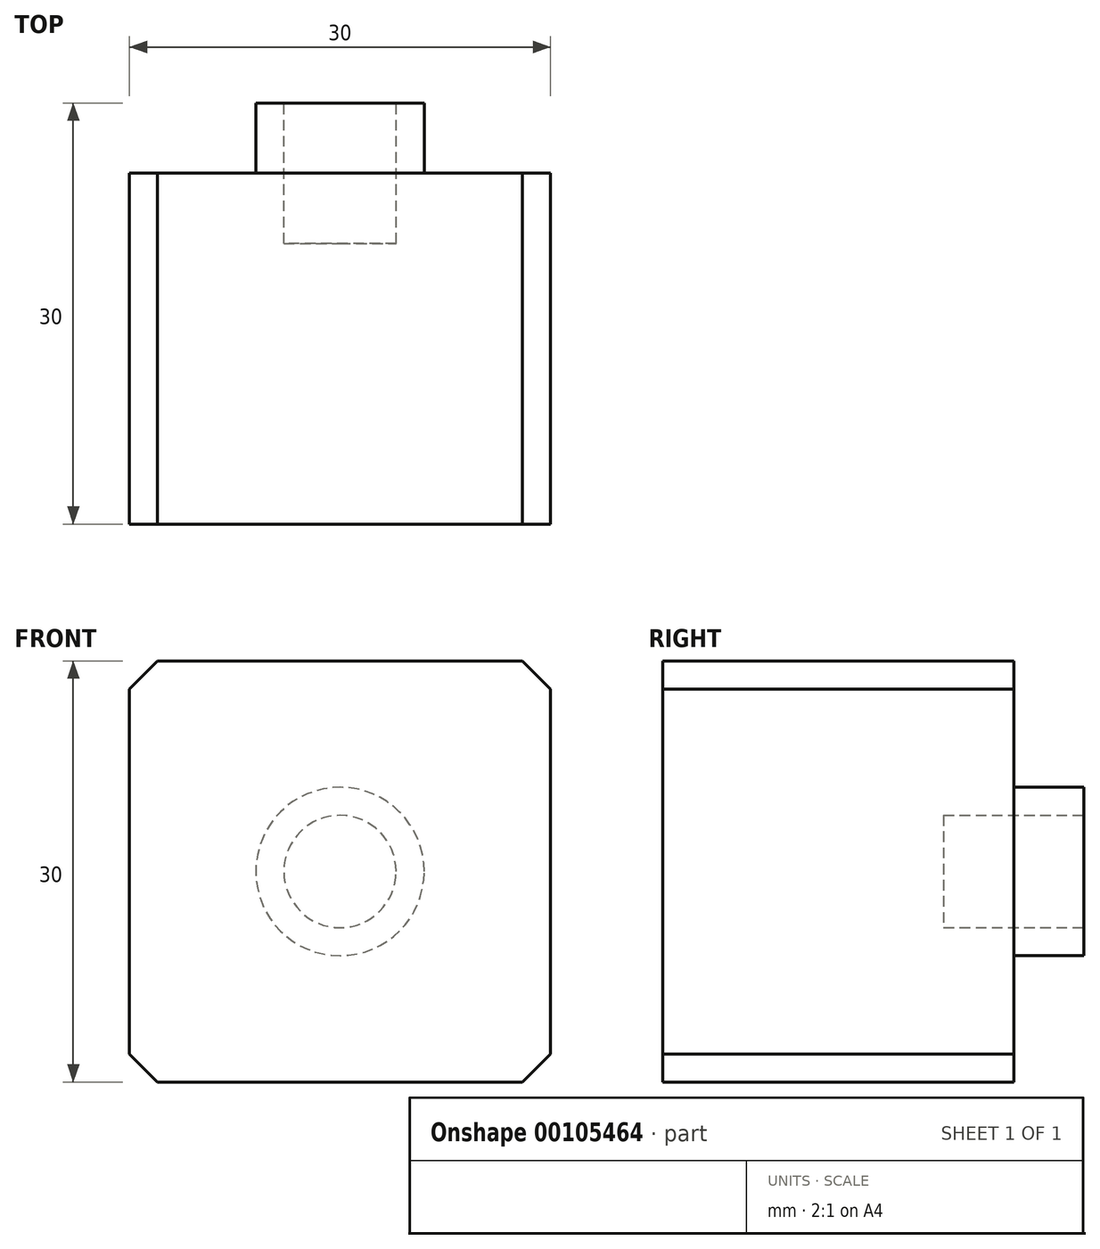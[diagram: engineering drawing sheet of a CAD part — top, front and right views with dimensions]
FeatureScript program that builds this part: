
annotation { "Feature Type Name" : "Feature", "Feature Type Description" : "" }
export const myFeature = defineFeature(function(context is Context, id is Id, definition is map)
    precondition{}
    {
        {
            var Q0;
            Q0=qCreatedBy(makeId("Front.planeOp"),FACE);
            var sketch = newSketch(context, id + "F0", { "sketchPlane" : qUnion([Q0])});
            skLineSegment(sketch, "E0.bottom", {"start": v(-12.17, 11.48) * mm, "end": v(17.83, 11.48) * mm});
            skLineSegment(sketch, "E0.top", {"start": v(-12.17, -18.52) * mm, "end": v(17.83, -18.52) * mm});
            skLineSegment(sketch, "E0.left", {"start": v(-12.17, 11.48) * mm, "end": v(-12.17, -18.52) * mm});
            skLineSegment(sketch, "E0.right", {"start": v(17.83, 11.48) * mm, "end": v(17.83, -18.52) * mm});
            skSolve(sketch);
        }
        {
            var Q0;
            Q0=makeQuery(id+"F0.imprint","IMPRINT",FACE,{"disambiguationData":[TD([[makeQuery(id+"F0.imprint","IMPRINT",EDGE,{"derivedFrom":sQuery(id+"F0.wireOp",EDGE,"E0.bottom")}),-1.0]])]});
            extrude(context, id + "F1", {"entities" : qUnion([Q0]), "depth" : 25 * mm});
        }
        {
            var Q0;
            Q0=makeQuery(id+"F1.opExtrude","CAP_FACE",FACE,{"disambiguationData":[OSD([sQuery(id+"F0.wireOp",EDGE,"E0.bottom"),sQuery(id+"F0.wireOp",EDGE,"E0.top"),sQuery(id+"F0.wireOp",EDGE,"E0.left"),sQuery(id+"F0.wireOp",EDGE,"E0.right")])],"isStart":true});
            var sketch = newSketch(context, id + "F2", { "sketchPlane" : qUnion([Q0])});
            skCircle(sketch, "E1", {"center": v(-2.83, -3.52) * mm, "radius": 4 * mm});
            skPoint(sketch, "E1.centerSnap0", {"position": v(12.17, -3.52) * mm});
            skPoint(sketch, "E1.centerSnap1", {"position": v(-2.83, 11.48) * mm});
            skSolve(sketch);
        }
        {
            var Q0;
            Q0=makeQuery(id+"F1.opExtrude","CAP_FACE",FACE,{"disambiguationData":[OSD([sQuery(id+"F0.wireOp",EDGE,"E0.bottom"),sQuery(id+"F0.wireOp",EDGE,"E0.top"),sQuery(id+"F0.wireOp",EDGE,"E0.left"),sQuery(id+"F0.wireOp",EDGE,"E0.right")])],"isStart":true});
            var sketch = newSketch(context, id + "F3", { "sketchPlane" : qUnion([Q0])});
            skCircle(sketch, "E2", {"center": v(-2.83, -3.52) * mm, "radius": 6 * mm});
            skPoint(sketch, "E2.centerSnap0", {"position": v(-2.83, 11.48) * mm});
            skPoint(sketch, "E2.centerSnap1", {"position": v(12.17, -3.52) * mm});
            skSolve(sketch);
        }
        {
            var Q0;
            Q0=makeQuery(id+"F3.imprint","IMPRINT",FACE,{"disambiguationData":[TD([[makeQuery(id+"F3.imprint","IMPRINT",EDGE,{"derivedFrom":sQuery(id+"F3.wireOp",EDGE,"E2")}),1.0]])]});
            var Q1;
            Q1=sQuery(id+"F3.wireOp",EDGE,"E2");
            extrude(context, id + "F4", {"entities" : qUnion([Q0]), "operationType" : NewBodyOperationType.ADD, "surfaceEntities" : qUnion([Q1]), "depth" : 5 * mm});
        }
        {
            var Q0;
            Q0=makeQuery(id+"F1.opExtrude","SWEPT_EDGE",EDGE,{"disambiguationData":[OSD([sQuery(id+"F0.wireOp",EDGE,"E0.bottom"),sQuery(id+"F0.wireOp",EDGE,"E0.right")])]});
            chamfer(context, id + "F5", {"entities" : qUnion([Q0]), "width" : 2 * mm, "tangentPropagation" : true});
        }
        {
            var Q0;
            Q0=makeQuery(id+"F1.opExtrude","SWEPT_EDGE",EDGE,{"disambiguationData":[OSD([sQuery(id+"F0.wireOp",EDGE,"E0.bottom"),sQuery(id+"F0.wireOp",EDGE,"E0.left")])]});
            chamfer(context, id + "F6", {"entities" : qUnion([Q0]), "width" : 2 * mm, "tangentPropagation" : true});
        }
        {
            var Q0;
            Q0=makeQuery(id+"F1.opExtrude","SWEPT_EDGE",EDGE,{"disambiguationData":[OSD([sQuery(id+"F0.wireOp",EDGE,"E0.top"),sQuery(id+"F0.wireOp",EDGE,"E0.left")])]});
            var Q1;
            Q1=makeQuery(id+"F1.opExtrude","SWEPT_EDGE",EDGE,{"disambiguationData":[OSD([sQuery(id+"F0.wireOp",EDGE,"E0.top"),sQuery(id+"F0.wireOp",EDGE,"E0.right")])]});
            chamfer(context, id + "F7", {"entities" : qUnion([Q0, Q1]), "width" : 2 * mm, "tangentPropagation" : true});
        }
        {
            var Q0;
            Q0=makeQuery(id+"F2.imprint","IMPRINT",FACE,{"disambiguationData":[TD([[makeQuery(id+"F2.imprint","IMPRINT",EDGE,{"derivedFrom":sQuery(id+"F2.wireOp",EDGE,"E1")}),1.0]])]});
            extrude(context, id + "F8", {"entities" : qUnion([Q0]), "operationType" : NewBodyOperationType.REMOVE, "oppositeDirection" : true, "depth" : 5 * mm});
        }
        {
            var Q0;
            Q0=makeQuery(id+"F4.opExtrude","CAP_FACE",FACE,{"disambiguationData":[OSD([sQuery(id+"F3.wireOp",EDGE,"E2")])],"isStart":false});
            var sketch = newSketch(context, id + "F9", { "sketchPlane" : qUnion([Q0])});
            skCircle(sketch, "E3", {"center": v(-2.83, -3.52) * mm, "radius": 4 * mm});
            skSolve(sketch);
        }
        {
            var Q0;
            Q0=makeQuery(id+"F9.imprint","IMPRINT",FACE,{"disambiguationData":[TD([[makeQuery(id+"F9.imprint","IMPRINT",EDGE,{"derivedFrom":sQuery(id+"F9.wireOp",EDGE,"E3")}),1.0]])]});
            extrude(context, id + "F10", {"entities" : qUnion([Q0]), "operationType" : NewBodyOperationType.REMOVE, "oppositeDirection" : true, "depth" : 5 * mm});
        }
    });
